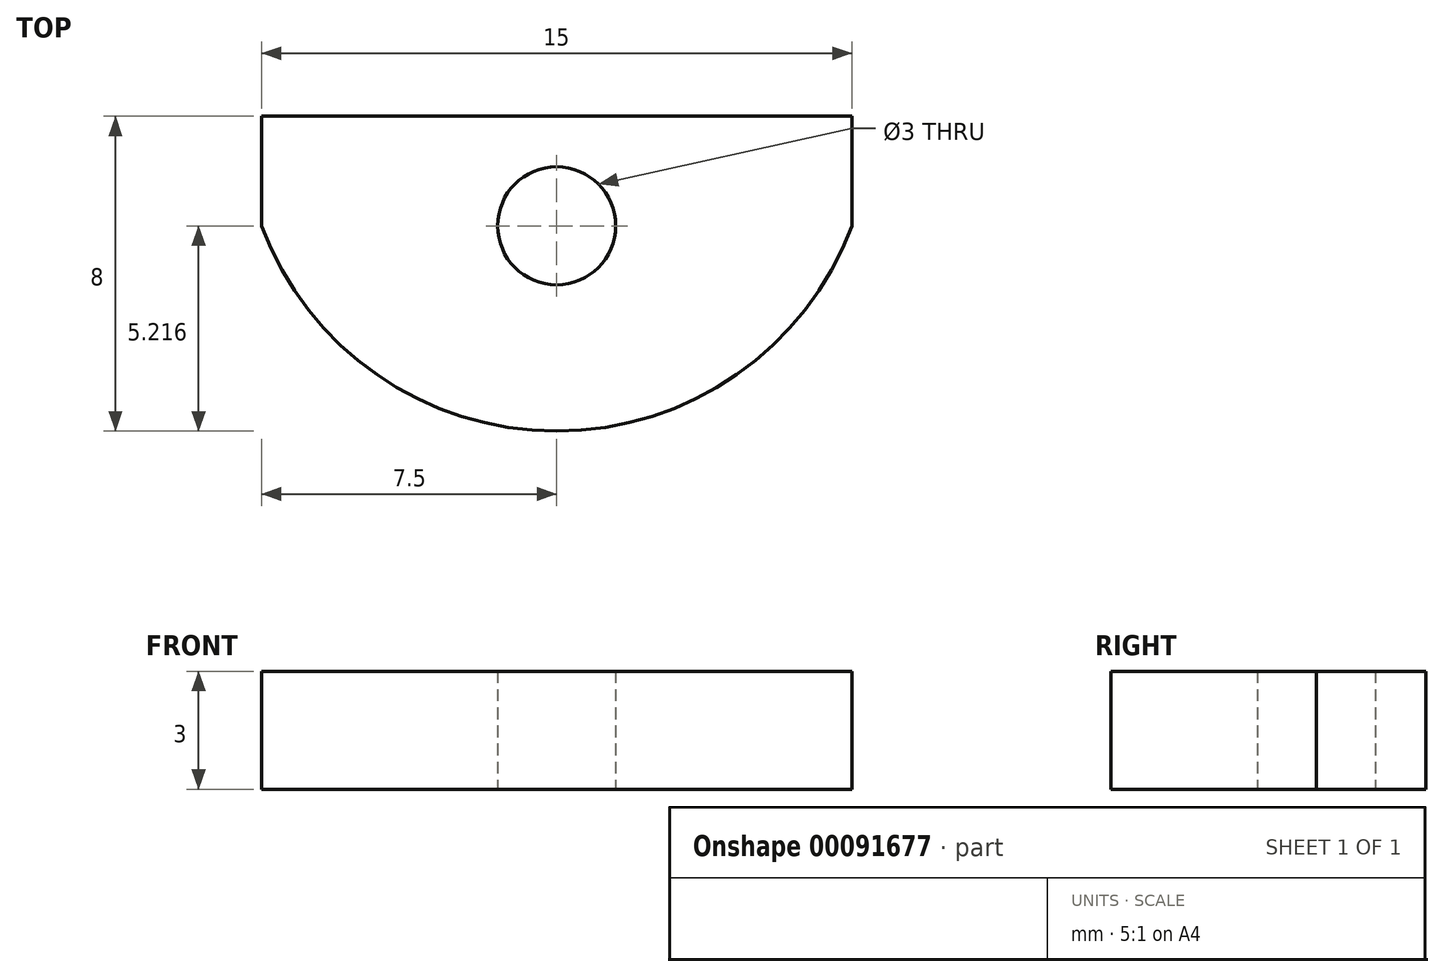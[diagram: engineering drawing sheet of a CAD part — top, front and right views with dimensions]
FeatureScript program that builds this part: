
annotation { "Feature Type Name" : "Feature", "Feature Type Description" : "" }
export const myFeature = defineFeature(function(context is Context, id is Id, definition is map)
    precondition{}
    {
        {
            var Q0;
            Q0=qCreatedBy(makeId("Top.planeOp"),FACE);
            var sketch = newSketch(context, id + "F0", { "sketchPlane" : qUnion([Q0])});
            skArc(sketch, "E0", {"start": v(-7.5, -2.78) * mm, "mid": v(0, -8) * mm, "end": v(7.5, -2.78) * mm});
            skLineSegment(sketch, "E1", {"start": v(-7.5, 0) * mm, "end": v(7.5, 0) * mm});
            skLineSegment(sketch, "E2", {"start": v(-7.5, 0) * mm, "end": v(-7.5, -2.78) * mm});
            skLineSegment(sketch, "E3", {"start": v(7.5, 0) * mm, "end": v(7.5, -2.78) * mm});
            skSolve(sketch);
        }
        {
            var Q0;
            Q0=makeQuery(id+"F0.imprint","IMPRINT",FACE,{"disambiguationData":[TD([[makeQuery(id+"F0.imprint","IMPRINT",EDGE,{"derivedFrom":sQuery(id+"F0.wireOp",EDGE,"E0")}),1.0]])]});
            extrude(context, id + "F1", {"entities" : qUnion([Q0]), "depth" : 3 * mm});
        }
        {
            var Q0;
            Q0=makeQuery(id+"F1.opExtrude","CAP_FACE",FACE,{"disambiguationData":[OSD([sQuery(id+"F0.wireOp",EDGE,"E0"),sQuery(id+"F0.wireOp",EDGE,"E1"),sQuery(id+"F0.wireOp",EDGE,"E2"),sQuery(id+"F0.wireOp",EDGE,"E3")])],"isStart":true});
            var sketch = newSketch(context, id + "F2", { "sketchPlane" : qUnion([Q0])});
            skCircle(sketch, "E4", {"center": v(0, 2.78) * mm, "radius": 1.5 * mm});
            skSolve(sketch);
        }
        {
            var Q0;
            Q0 = qSketchRegion(id + "F2", true);
            extrude(context, id + "F3", {"entities" : qUnion([Q0]), "operationType" : NewBodyOperationType.REMOVE, "oppositeDirection" : true, "depth" : 5 * mm});
        }
    });
